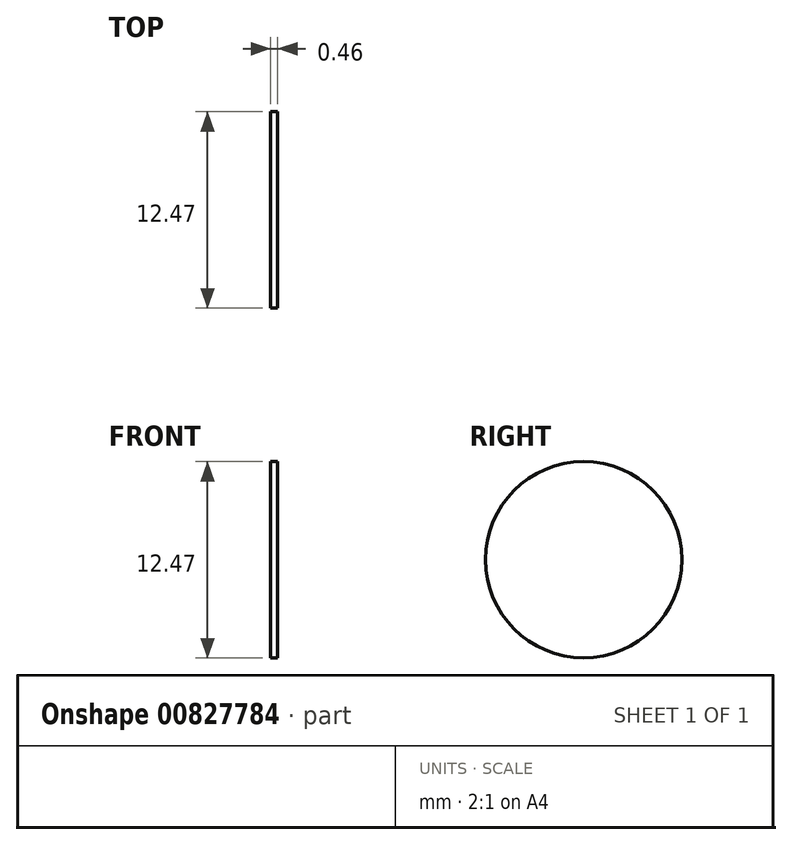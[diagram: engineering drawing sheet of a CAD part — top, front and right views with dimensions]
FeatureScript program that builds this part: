
annotation { "Feature Type Name" : "Feature", "Feature Type Description" : "" }
export const myFeature = defineFeature(function(context is Context, id is Id, definition is map)
    precondition{}
    {
        {
            var Q0;
            Q0=qCreatedBy(makeId("Right.planeOp"),FACE);
            var sketch = newSketch(context, id + "F0", { "sketchPlane" : qUnion([Q0])});
            skCircle(sketch, "E0", {"center": v(-8, -45.88) * mm, "radius": 6.23 * mm});
            skSolve(sketch);
        }
        {
            var Q0;
            Q0=makeQuery(id+"F0.imprint","IMPRINT",FACE,{"disambiguationData":[TD([[makeQuery(id+"F0.imprint","IMPRINT",EDGE,{"derivedFrom":sQuery(id+"F0.wireOp",EDGE,"E0")}),1.0]])]});
            extrude(context, id + "F1", {"entities" : qUnion([Q0]), "depth" : 0.46 * mm, "offsetDistance" : 25.4 * mm});
        }
    });
